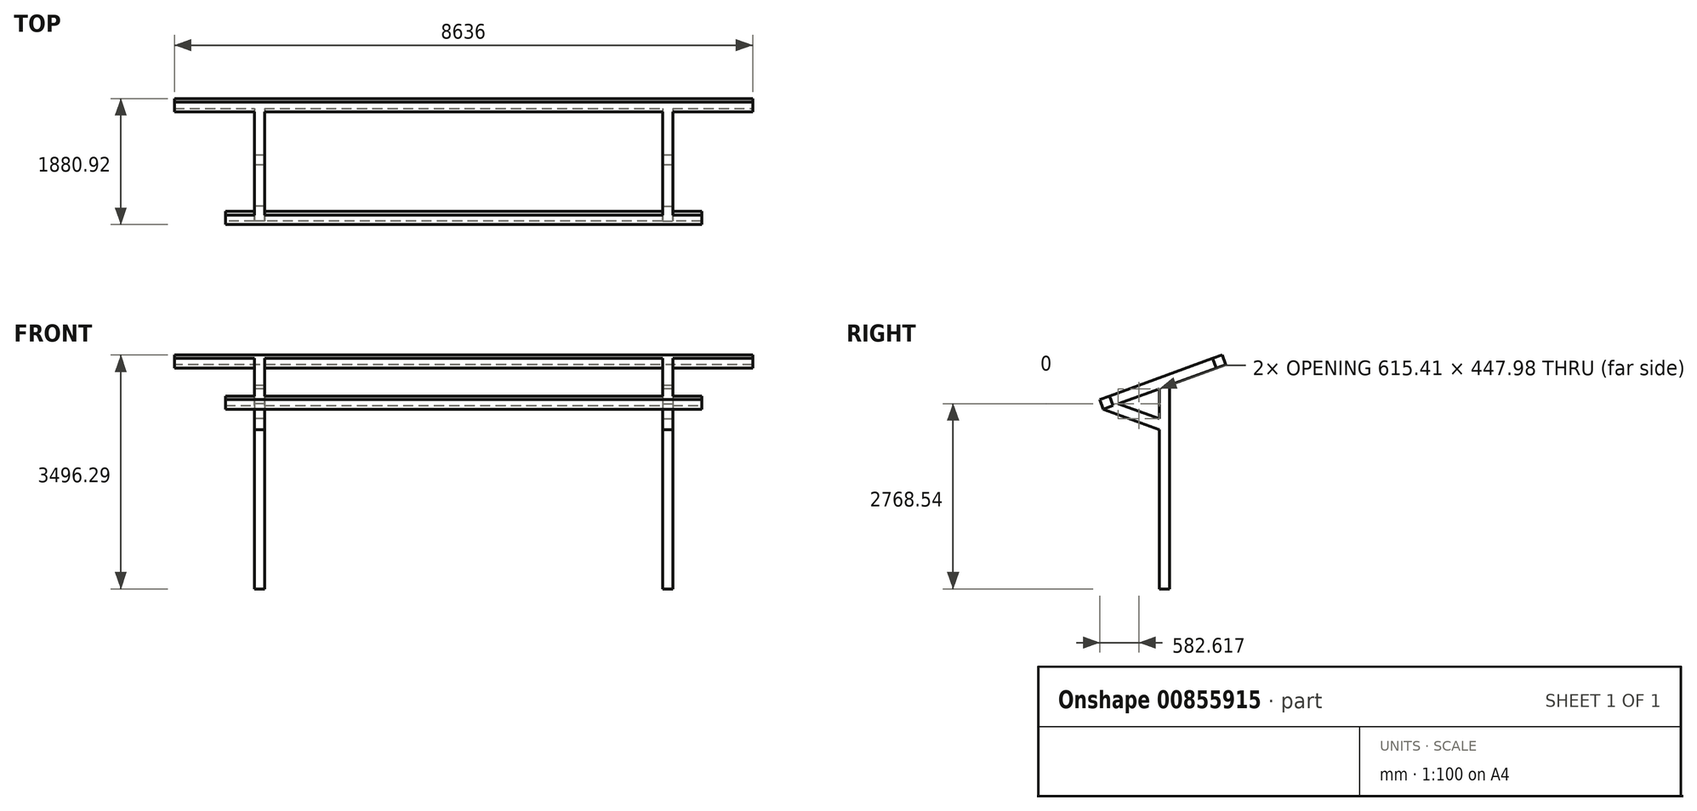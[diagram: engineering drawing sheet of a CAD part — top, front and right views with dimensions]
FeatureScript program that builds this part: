
annotation { "Feature Type Name" : "Feature", "Feature Type Description" : "" }
export const myFeature = defineFeature(function(context is Context, id is Id, definition is map)
    precondition{}
    {
        {
            var Q0;
            Q0=qCreatedBy(makeId("Top.planeOp"),FACE);
            var sketch = newSketch(context, id + "F0", { "sketchPlane" : qUnion([Q0])});
            skLineSegment(sketch, "E0.bottom", {"start": v(2971.8, 76.2) * mm, "end": v(3124.2, 76.2) * mm});
            skLineSegment(sketch, "E0.top", {"start": v(2971.8, -76.2) * mm, "end": v(3124.2, -76.2) * mm});
            skLineSegment(sketch, "E0.left", {"start": v(2971.8, 76.2) * mm, "end": v(2971.8, -76.2) * mm});
            skLineSegment(sketch, "E0.right", {"start": v(3124.2, 76.2) * mm, "end": v(3124.2, -76.2) * mm});
            skLineSegment(sketch, "E1", {"start": v(0, 0) * mm, "end": v(98.94, 0) * mm, "construction": true});
            skLineSegment(sketch, "E2", {"start": v(3048, 76.2) * mm, "end": v(3048, -76.2) * mm, "construction": true});
            skLineSegment(sketch, "E3", {"start": v(0, 65.52) * mm, "end": v(0, -66.7) * mm, "construction": true});
            skLineSegment(sketch, "E4.MirrorCS", {"start": v(3124.2, 76.2) * mm, "end": v(2971.8, 76.2) * mm});
            skLineSegment(sketch, "E5.MirrorCS", {"start": v(3124.2, -76.2) * mm, "end": v(2971.8, -76.2) * mm});
            skLineSegment(sketch, "E6.MirrorCS", {"start": v(-2971.8, 76.2) * mm, "end": v(-2971.8, -76.2) * mm});
            skLineSegment(sketch, "E7.MirrorCS", {"start": v(-3124.2, 76.2) * mm, "end": v(-2971.8, 76.2) * mm});
            skLineSegment(sketch, "E8.MirrorCS", {"start": v(-3124.2, 76.2) * mm, "end": v(-3124.2, -76.2) * mm});
            skLineSegment(sketch, "E9.MirrorCS", {"start": v(-2971.8, -76.2) * mm, "end": v(-3124.2, -76.2) * mm});
            skSolve(sketch);
        }
        {
            var Q0;
            Q0=makeQuery(id+"F0.imprint","IMPRINT",FACE,{"disambiguationData":[TD([[makeQuery(id+"F0.imprint","IMPRINT",EDGE,{"derivedFrom":sQuery(id+"F0.wireOp",EDGE,"E6.MirrorCS")}),-1.0]])]});
            var Q1;
            Q1=makeQuery(id+"F0.imprint","IMPRINT",FACE,{"disambiguationData":[TD([[makeQuery(id+"F0.imprint","IMPRINT",EDGE,{"derivedFrom":sQuery(id+"F0.wireOp",EDGE,"E0.bottom")}),-1.0]])]});
            extrude(context, id + "F1", {"entities" : qUnion([Q0, Q1]), "depth" : 3048 * mm, "offsetDistance" : 25.4 * mm});
        }
        {
            var Q0;
            Q0=makeQuery(id+"F1.opExtrude","CAP_EDGE",EDGE,{"disambiguationData":[OSD([sQuery(id+"F0.wireOp",EDGE,"E0.top")])],"isStart":false});
            chamfer(context, id + "F2", {"entities" : qUnion([Q0]), "chamferType" : ChamferType.OFFSET_ANGLE, "width" : 152.4 * mm, "oppositeDirection" : false, "angle" : 20 * degree, "tangentPropagation" : true});
        }
        {
            var Q0;
            Q0=makeQuery(id+"F1.opExtrude","CAP_EDGE",EDGE,{"disambiguationData":[OSD([sQuery(id+"F0.wireOp",EDGE,"E9.MirrorCS")])],"isStart":false});
            chamfer(context, id + "F3", {"entities" : qUnion([Q0]), "chamferType" : ChamferType.OFFSET_ANGLE, "width" : 152.4 * mm, "oppositeDirection" : true, "angle" : 20 * degree, "tangentPropagation" : true});
        }
        {
            var Q0;
            Q0=makeQuery(id+"F1.opExtrude","SWEPT_FACE",FACE,{"disambiguationData":[OSD([sQuery(id+"F0.wireOp",EDGE,"E0.right")])]});
            var sketch = newSketch(context, id + "F4", { "sketchPlane" : qUnion([Q0])});
            skLineSegment(sketch, "E10", {"start": v(-914.4, 2687.45) * mm, "end": v(914.4, 3353.08) * mm});
            skLineSegment(sketch, "E11", {"start": v(0, 3020.27) * mm, "end": v(0, 3340.18) * mm, "construction": true});
            skLineSegment(sketch, "E12", {"start": v(-966.52, 2830.66) * mm, "end": v(862.28, 3496.29) * mm});
            skLineSegment(sketch, "E13", {"start": v(862.28, 3496.29) * mm, "end": v(914.4, 3353.08) * mm});
            skLineSegment(sketch, "E14", {"start": v(-966.52, 2830.66) * mm, "end": v(-914.4, 2687.45) * mm});
            skSolve(sketch);
        }
        {
            var Q0;
            Q0=makeQuery(id+"F4.imprint","IMPRINT",FACE,{"disambiguationData":[TD([[makeQuery(id+"F4.imprint","IMPRINT",EDGE,{"derivedFrom":sQuery(id+"F4.wireOp",EDGE,"E12")}),-1.0]])]});
            extrude(context, id + "F5", {"entities" : qUnion([Q0]), "oppositeDirection" : true, "depth" : 152.4 * mm, "offsetDistance" : 25.4 * mm});
        }
        {
            var Q0;
            Q0=makeQuery(id+"F5.opExtrude","SWEPT_BODY",BODY,{"disambiguationData":[OSD([sQuery(id+"F4.wireOp",EDGE,"E10"),sQuery(id+"F4.wireOp",EDGE,"E12"),sQuery(id+"F4.wireOp",EDGE,"E13"),sQuery(id+"F4.wireOp",EDGE,"E14")])]});
            var Q1;
            Q1=qCreatedBy(makeId("Right.planeOp"),FACE);
            mirror(context, id + "F6", {"entities" : qUnion([Q0]), "mirrorPlane" : qUnion([Q1])});
        }
        {
            var Q0;
            Q0=makeQuery(id+"F5.opExtrude","SWEPT_FACE",FACE,{"disambiguationData":[OSD([sQuery(id+"F4.wireOp",EDGE,"E12")])]});
            var sketch = newSketch(context, id + "F7", { "sketchPlane" : qUnion([Q0])});
            skLineSegment(sketch, "E15", {"start": v(-3556, 59.9) * mm, "end": v(3556, 59.9) * mm});
            skLineSegment(sketch, "E16", {"start": v(0, 0) * mm, "end": v(0, 349.84) * mm, "construction": true});
            skLineSegment(sketch, "E17", {"start": v(-3556, 212.3) * mm, "end": v(3556, 212.3) * mm});
            skLineSegment(sketch, "E18", {"start": v(3556, 212.3) * mm, "end": v(3556, 59.9) * mm});
            skLineSegment(sketch, "E19", {"start": v(-3556, 212.3) * mm, "end": v(-3556, 59.9) * mm});
            skLineSegment(sketch, "E20.bottom", {"start": v(-4318, 2006.08) * mm, "end": v(4318, 2006.08) * mm});
            skLineSegment(sketch, "E20.top", {"start": v(-4318, 1853.68) * mm, "end": v(4318, 1853.68) * mm});
            skLineSegment(sketch, "E20.left", {"start": v(-4318, 2006.08) * mm, "end": v(-4318, 1853.68) * mm});
            skLineSegment(sketch, "E20.right", {"start": v(4318, 2006.08) * mm, "end": v(4318, 1853.68) * mm});
            skSolve(sketch);
        }
        {
            var Q0;
            Q0 = qSketchRegion(id + "F7", true);
            extrude(context, id + "F8", {"entities" : qUnion([Q0]), "oppositeDirection" : true, "depth" : 152.4 * mm, "offsetDistance" : 25.4 * mm});
        }
        {
            var Q0;
            Q0=makeQuery(id+"F6.opPattern","COPY",BODY,{"derivedFrom":makeQuery(id+"F5.opExtrude","SWEPT_BODY",BODY,{"disambiguationData":[OSD([sQuery(id+"F4.wireOp",EDGE,"E10"),sQuery(id+"F4.wireOp",EDGE,"E12"),sQuery(id+"F4.wireOp",EDGE,"E13"),sQuery(id+"F4.wireOp",EDGE,"E14")])]}),"instanceName":"1"});
            var Q1;
            Q1=makeQuery(id+"F8.opExtrude","SWEPT_BODY",BODY,{"disambiguationData":[OSD([sQuery(id+"F7.wireOp",EDGE,"E20.bottom"),sQuery(id+"F7.wireOp",EDGE,"E20.top"),sQuery(id+"F7.wireOp",EDGE,"E20.left"),sQuery(id+"F7.wireOp",EDGE,"E20.right")])]});
            var Q2;
            Q2=makeQuery(id+"F5.opExtrude","SWEPT_BODY",BODY,{"disambiguationData":[OSD([sQuery(id+"F4.wireOp",EDGE,"E10"),sQuery(id+"F4.wireOp",EDGE,"E12"),sQuery(id+"F4.wireOp",EDGE,"E13"),sQuery(id+"F4.wireOp",EDGE,"E14")])]});
            var Q3;
            Q3=makeQuery(id+"F8.opExtrude","SWEPT_BODY",BODY,{"disambiguationData":[OSD([sQuery(id+"F7.wireOp",EDGE,"E15"),sQuery(id+"F7.wireOp",EDGE,"E17"),sQuery(id+"F7.wireOp",EDGE,"E18"),sQuery(id+"F7.wireOp",EDGE,"E19")])]});
            var Q4;
            Q4=makeQuery(id+"F1.opExtrude","SWEPT_BODY",BODY,{"disambiguationData":[OSD([sQuery(id+"F0.wireOp",EDGE,"E6.MirrorCS"),sQuery(id+"F0.wireOp",EDGE,"E7.MirrorCS"),sQuery(id+"F0.wireOp",EDGE,"E8.MirrorCS"),sQuery(id+"F0.wireOp",EDGE,"E9.MirrorCS")])]});
            var Q5;
            Q5=makeQuery(id+"F1.opExtrude","SWEPT_BODY",BODY,{"disambiguationData":[OSD([sQuery(id+"F0.wireOp",EDGE,"E0.bottom"),sQuery(id+"F0.wireOp",EDGE,"E0.top"),sQuery(id+"F0.wireOp",EDGE,"E0.left"),sQuery(id+"F0.wireOp",EDGE,"E0.right")])]});
            booleanBodies(context, id + "F9", {"operationType" : BooleanOperationType.UNION, "tools" : qUnion([Q0, Q1, Q2, Q3, Q4, Q5])});
        }
        {
            var Q0;
            Q0=makeQuery(id+"F9.opBoolean","MERGE",FACE,{"derivedFrom":[makeQuery(id+"F1.opExtrude","SWEPT_FACE",FACE,{"disambiguationData":[OSD([sQuery(id+"F0.wireOp",EDGE,"E0.right")])]}),makeQuery(id+"F5.opExtrude","CAP_FACE",FACE,{"disambiguationData":[OSD([sQuery(id+"F4.wireOp",EDGE,"E10"),sQuery(id+"F4.wireOp",EDGE,"E12"),sQuery(id+"F4.wireOp",EDGE,"E13"),sQuery(id+"F4.wireOp",EDGE,"E14")])],"isStart":true})]});
            var sketch = newSketch(context, id + "F10", { "sketchPlane" : qUnion([Q0])});
            skLineSegment(sketch, "E21", {"start": v(-914.4, 2687.45) * mm, "end": v(-76.2, 2382.37) * mm});
            skLineSegment(sketch, "E22", {"start": v(-76.2, 2382.37) * mm, "end": v(-76.2, 2544.55) * mm});
            skLineSegment(sketch, "E23", {"start": v(-76.2, 2544.55) * mm, "end": v(-691.6, 2768.54) * mm});
            skLineSegment(sketch, "E24", {"start": v(-691.6, 2768.54) * mm, "end": v(-914.4, 2687.45) * mm});
            skSolve(sketch);
        }
        {
            var Q0;
            {var subQ9=sQuery(id+"F10.wireOp",EDGE,"E21");Q0=makeQuery(id+"F10.imprint","IMPRINT",FACE,{"disambiguationData":[TD([[makeQuery(id+"F10.imprint","IMPRINT",EDGE,{"derivedFrom":subQ9}),1.0]])]});}
            extrude(context, id + "F11", {"entities" : qUnion([Q0]), "oppositeDirection" : true, "depth" : 152.4 * mm, "offsetDistance" : 25.4 * mm});
        }
        {
            var Q0;
            Q0=makeQuery(id+"F11.opExtrude","SWEPT_BODY",BODY,{"disambiguationData":[OSD([sQuery(id+"F10.wireOp",EDGE,"E21"),sQuery(id+"F10.wireOp",EDGE,"E22"),sQuery(id+"F10.wireOp",EDGE,"E23"),sQuery(id+"F10.wireOp",EDGE,"E24")])]});
            var Q1;
            Q1=qCreatedBy(makeId("Right.planeOp"),FACE);
            mirror(context, id + "F12", {"operationType" : NewBodyOperationType.ADD, "entities" : qUnion([Q0]), "mirrorPlane" : qUnion([Q1])});
        }
    });
